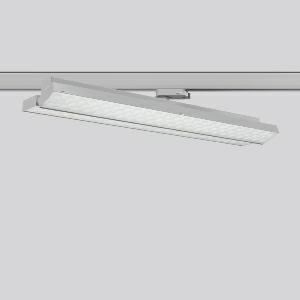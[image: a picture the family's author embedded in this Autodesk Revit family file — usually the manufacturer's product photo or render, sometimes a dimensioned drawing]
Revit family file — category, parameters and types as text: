
# Revit family: tx-move_742162_004_84eb
name_source: partatom
category: Lighting Fixtures
units: mm (PartAtom-declared; Revit-internal decimal feet)

## family parameters
Cut with Voids When Loaded = No
Host = Face
Light Source = No
Part Type = Normal
Room Calculation Point = No
Round Connector Dimension = Use Diameter
Shared = No

## types (1)
- MultiLumen 1 (1 x LED Modul 830, 2925 lm, 3000)
    Apparent Load = 41 VA
    CIE Flux Codes = 77 96 99 100 100
    Color Rendering = 80
    Color Temperature = 3000
    Default Elevation = 1800 mm
    Description = Series: TX-MOVE
Multifunctional surface-mounted spotlight for area lighting. Very flat design. Housing: sheet steel, powder-coated. Rotation range: 356°. Swivel range: 90°. Consistent alignment possible with visible tilt scale. High-efficiency LED units with optimum light control thanks to clear plastic (PC) lens optics. Spezielle Mikrostrukturen reduzieren Gelbsaum. Symmetrical light distribution. With multi adaptor for 3-circuit tracks 230 V. Suitable for Track on ceiling. MultiLumen: Luminous flux adjustable in 3 steps. Factory setting is the highest luminous flux. Environmentally friendly and resource-saving due to replaceable and recyclable components. 
Colour: silver, matt (approx. RAL 9006)
Length: 570 mm
Width: 119 mm
Height: 92 mm
Lamp: LED
Socket: without socket
Colour temperature: 3000K
Colour rendering index (CRI): 80
System power: 41 W
Rated luminous flux: 5850 lm
Luminous efficiency: 143 lm/W
System power 2: 57 W
Rated luminous flux 2: 7950 lm
Luminous efficiency 2: 139 lm/W
System power 3: 73 W
Rated luminous flux 3: 9700 lm
Luminous efficiency 3: 133 lm/W
Control gear: Regulated power supply
Protection class: I
Type of protection: IP 20
    Height = 75 mm
    Lamp = 1 x LED Modul 830
    Lamp Light Flux = 2925 lm
    Lamp count = 1
    Length = 569 mm
    Lifetime = 50000 h
    Luminous efficacy = 143 lm/W
    Manufacturer = RZB
    ModVariant = No
    Model = 742162.004
    Mounting Place = Ceiling
    Mounting Type = Surface mounted
    Number of Poles = 1
    OnlyDefault = Yes
    Power Factor = 1
    Product Name = TX-MOVE
    Product group = Track mounted projectors
    ProductGroupID = 301
    Protection Class = Protection class I
    Protection Degree = IP 20
    RLX_Detail_Level = 1
    RLX_Emergency_Light_Flux = 0 lm
    RLX_Emergency_Type = 0
    RLX_Emergency_Type_DB = No
    RlxData = <blob elided: 33101 chars, md5=81a3775e>
    Socket = socket
    Standby Power = 0 W
    System Light Flux = 5850 lm
    System Power = 41 W
    Type Comments = MultiLumen 1
    Type Image = 742162.004.jpg
    URL = http://relux.com
    VarID = multilumen_1
    Voltage = 0 V
    Weight = 0.00 kg
    Width = 119 mm

## geometry (parser evidence)
native form markers: Blend x4, Sweep x16
no freeform markers — native parametric forms only
